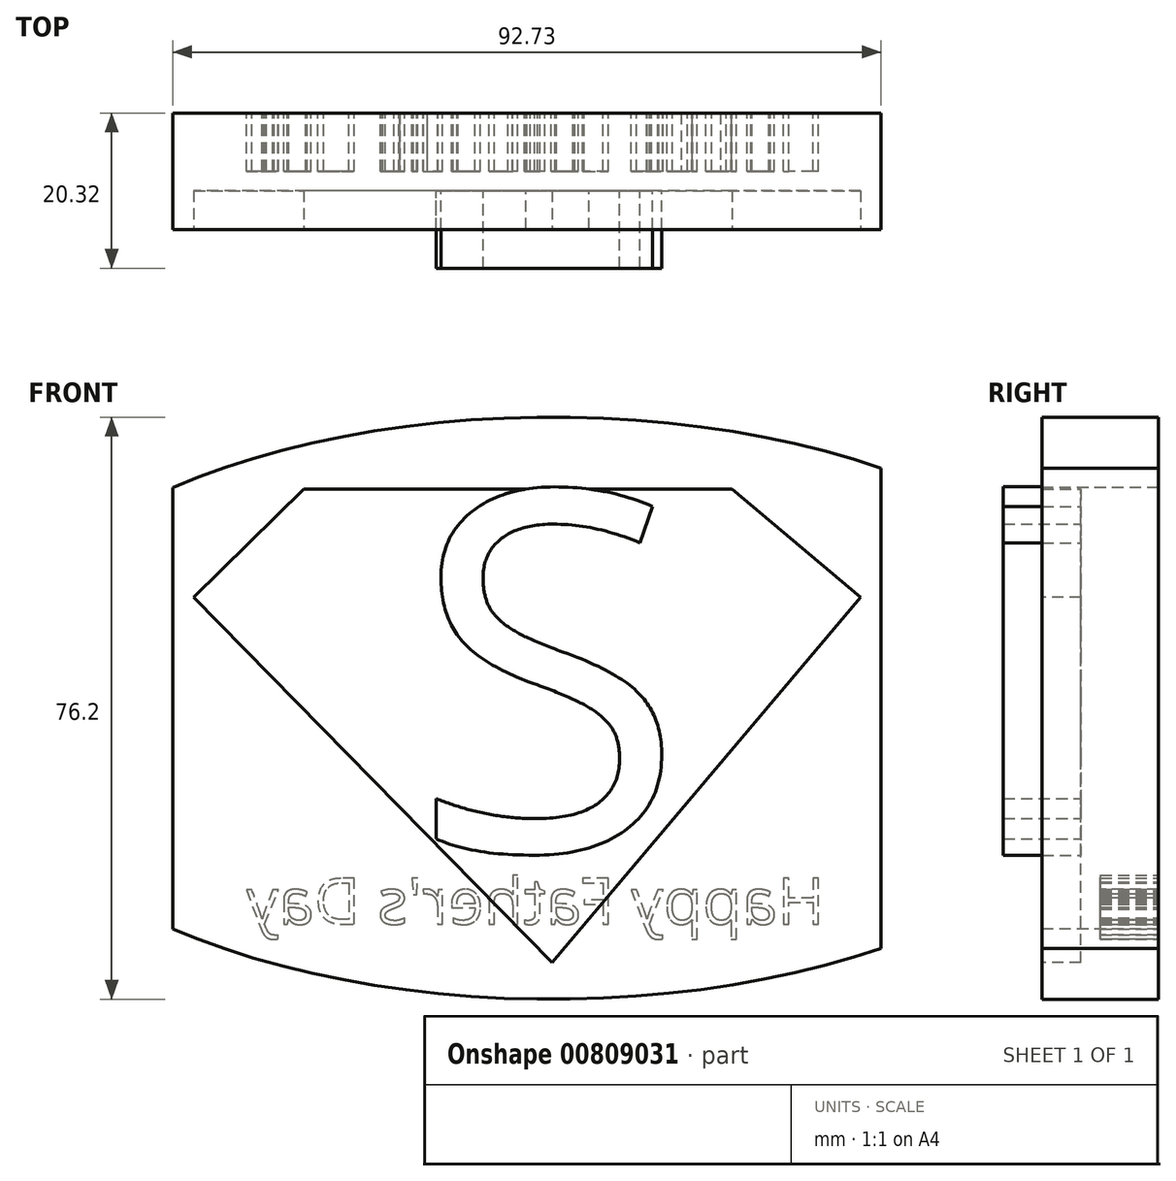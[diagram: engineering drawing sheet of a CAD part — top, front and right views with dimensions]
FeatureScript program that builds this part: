
annotation { "Feature Type Name" : "Feature", "Feature Type Description" : "" }
export const myFeature = defineFeature(function(context is Context, id is Id, definition is map)
    precondition{}
    {
        {
            var Q0;
            Q0=qCreatedBy(makeId("Front.planeOp"),FACE);
            var sketch = newSketch(context, id + "F0", { "sketchPlane" : qUnion([Q0])});
            skEllipse(sketch, "E0", {"center": v(0, 0) * mm, "majorRadius": 76.2 * mm, "minorRadius": 38.1 * mm, "majorAxis": v(-1, 0)});
            skSolve(sketch);
        }
        {
            var Q0;
            Q0 = qSketchRegion(id + "F0", true);
            extrude(context, id + "F1", {"entities" : qUnion([Q0]), "depth" : 15.24 * mm, "offsetDistance" : 25.4 * mm});
        }
        {
            var Q0;
            Q0=makeQuery(id+"F1.opExtrude","CAP_FACE",FACE,{"disambiguationData":[OSD([sQuery(id+"F0.wireOp",EDGE,"E0")])],"isStart":false});
            var sketch = newSketch(context, id + "F2", { "sketchPlane" : qUnion([Q0])});
            skLineSegment(sketch, "E1", {"start": v(0, -33.33) * mm, "end": v(-46.95, 14.55) * mm});
            skPoint(sketch, "E1.startSnap0", {"position": v(0, -38.1) * mm});
            skLineSegment(sketch, "E2", {"start": v(0, -33.33) * mm, "end": v(40.34, 14.55) * mm});
            skLineSegment(sketch, "E3", {"start": v(-46.95, 14.55) * mm, "end": v(-32.53, 28.69) * mm});
            skLineSegment(sketch, "E4", {"start": v(40.34, 14.55) * mm, "end": v(23.55, 28.69) * mm});
            skLineSegment(sketch, "E5", {"start": v(23.55, 28.69) * mm, "end": v(-32.53, 28.69) * mm});
            skText(sketch, "E6", { "text": "S", "fontName": "OpenSans-Regular.ttf"});
            const initialGuessF2  = {"E6": [-0.01785, -0.02037, 1, 0, 0.04905]};
            skSetInitialGuess(sketch, initialGuessF2);
            skSolve(sketch);
        }
        {
            var Q0;
            Q0=makeQuery(id+"F2.imprint","IMPRINT",FACE,{"disambiguationData":[TD([[makeQuery(id+"F2.imprint","IMPRINT",EDGE,{"derivedFrom":sQuery(id+"F2.wireOp",EDGE,"E6.sketch_text.stroke-0")}),-1.0]])]});
            var Q1;
            {var subQ9=sQuery(id+"F2.wireOp",EDGE,"E2");Q1=makeQuery(id+"F2.imprint","IMPRINT",FACE,{"disambiguationData":[TD([[makeQuery(id+"F2.imprint","IMPRINT",EDGE,{"derivedFrom":subQ9}),1.0]])]});}
            var Q2;
            {var subQ0=sQuery(id+"F2.wireOp",EDGE,"E3");Q2=makeQuery(id+"F2.imprint","IMPRINT",FACE,{"disambiguationData":[TD([[makeQuery(id+"F2.imprint","IMPRINT",EDGE,{"derivedFrom":subQ0}),-1.0]])]});}
            extrude(context, id + "F3", {"entities" : qUnion([Q0, Q1, Q2]), "operationType" : NewBodyOperationType.REMOVE, "oppositeDirection" : true, "depth" : 5.08 * mm, "offsetDistance" : 25.4 * mm});
        }
        {
            var Q0;
            Q0=makeQuery(id+"F3.boolean.opBoolean","COPY",FACE,{"derivedFrom":makeQuery(id+"F3.opExtrude","CAP_FACE",FACE,{"disambiguationData":[OSD([sQuery(id+"F2.wireOp",EDGE,"E1"),sQuery(id+"F2.wireOp",EDGE,"E2"),sQuery(id+"F2.wireOp",EDGE,"E3"),sQuery(id+"F2.wireOp",EDGE,"E4"),sQuery(id+"F2.wireOp",EDGE,"E5")])],"isStart":false})});
            var sketch = newSketch(context, id + "F4", { "sketchPlane" : qUnion([Q0])});
            skText(sketch, "E7", { "text": "S", "fontName": "OpenSans-Regular.ttf"});
            const initialGuessF4  = {"E7": [-0.01858, -0.0186, 1, 0, 0.0473]};
            skSetInitialGuess(sketch, initialGuessF4);
            skSolve(sketch);
        }
        {
            var Q0;
            Q0 = qSketchRegion(id + "F4", true);
            extrude(context, id + "F5", {"entities" : qUnion([Q0]), "operationType" : NewBodyOperationType.ADD, "depth" : 10.16 * mm, "offsetDistance" : 25.4 * mm});
        }
        {
            var Q0;
            Q0=makeQuery(id+"F1.opExtrude","CAP_FACE",FACE,{"disambiguationData":[OSD([sQuery(id+"F0.wireOp",EDGE,"E0")])],"isStart":false});
            var sketch = newSketch(context, id + "F6", { "sketchPlane" : qUnion([Q0])});
            skLineSegment(sketch, "E8", {"start": v(-49.67, 28.9) * mm, "end": v(-49.67, -28.9) * mm});
            skLineSegment(sketch, "E9", {"start": v(-49.67, -28.9) * mm, "end": v(-81.33, -28.9) * mm});
            skLineSegment(sketch, "E10", {"start": v(-81.33, -28.9) * mm, "end": v(-81.33, 28.69) * mm});
            skLineSegment(sketch, "E11", {"start": v(-81.33, 28.69) * mm, "end": v(-49.67, 28.9) * mm});
            skSolve(sketch);
        }
        {
            var Q0;
            Q0 = qSketchRegion(id + "F6", true);
            extrude(context, id + "F7", {"entities" : qUnion([Q0]), "operationType" : NewBodyOperationType.REMOVE, "oppositeDirection" : true, "depth" : 38.1 * mm, "offsetDistance" : 25.4 * mm});
        }
        {
            var Q0;
            Q0=makeQuery(id+"F1.opExtrude","CAP_FACE",FACE,{"disambiguationData":[OSD([sQuery(id+"F0.wireOp",EDGE,"E0")])],"isStart":false});
            var sketch = newSketch(context, id + "F8", { "sketchPlane" : qUnion([Q0])});
            skLineSegment(sketch, "E12", {"start": v(43.06, 31.43) * mm, "end": v(43.06, -31.43) * mm});
            skLineSegment(sketch, "E13", {"start": v(43.06, -31.43) * mm, "end": v(78.69, -28.9) * mm});
            skLineSegment(sketch, "E14", {"start": v(78.69, -28.9) * mm, "end": v(78.69, 32.53) * mm});
            skLineSegment(sketch, "E15", {"start": v(78.69, 32.53) * mm, "end": v(43.06, 31.43) * mm});
            skSolve(sketch);
        }
        {
            var Q0;
            Q0 = qSketchRegion(id + "F8", true);
            extrude(context, id + "F9", {"entities" : qUnion([Q0]), "operationType" : NewBodyOperationType.REMOVE, "oppositeDirection" : true, "depth" : 38.1 * mm, "offsetDistance" : 25.4 * mm});
        }
        {
            var Q0;
            Q0=makeQuery(id+"F1.opExtrude","CAP_FACE",FACE,{"disambiguationData":[OSD([sQuery(id+"F0.wireOp",EDGE,"E0")])],"isStart":true});
            var sketch = newSketch(context, id + "F10", { "sketchPlane" : qUnion([Q0])});
            skText(sketch, "E16", { "text": "Happy Father\'s Day", "fontName": "OpenSans-Regular.ttf"});
            const initialGuessF10  = {"E16": [-0.03564, -0.02826, 1, 0, 0.00603]};
            skSetInitialGuess(sketch, initialGuessF10);
            skSolve(sketch);
        }
        {
            var Q0;
            Q0 = qSketchRegion(id + "F10", true);
            extrude(context, id + "F11", {"entities" : qUnion([Q0]), "operationType" : NewBodyOperationType.REMOVE, "oppositeDirection" : true, "depth" : 7.62 * mm, "offsetDistance" : 25.4 * mm});
        }
    });
